# Revit family: BAS-IP_Вызывная панель_AV-04AFDI
name_source: partatom
category: Устройства связи
units: mm (PartAtom-declared; Revit-internal decimal feet)

## family parameters
Всегда вертикально = Да
На основе рабочей плоскости = Нет
Общий = Нет
При загрузке вырезать с полостями = Нет
Размер круглого соединителя = Использовать диаметр
Сохранять ориентацию аннотаций = Нет
Тип детали = Нормальный
Точка расчета площади = Нет

## types (3) — shared parameters
ADSK_Единица измерения = шт.
ADSK_Завод-изготовитель = BAS-IP
ADSK_Количество = 1
ADSK_Наименование = Индивидуальная панель с возможностью подключения индукционной петли
IK-код = IK08
Дисплей = Нет
Изготовитель = BAS-IP
Класс степени защиты = IP65
Корпус = Алюминий
Питание = IEEE 803.2af PoE, +12 В постоянного тока
Потребление питания = 6,5 Вт, в режиме ожидания - 3,6 Вт
Размер под установку = 85 × 180 × 45 мм
Размер самой панели = 95 x 190 x 27 мм
Температурный режим = -40 – +65 °С
Тип панели = Индивидуальная
Тип установки = Скрытого монтажа

## per-type parameters (varying)
| type | ADSK_Марка | ADSK_Материал |
| Серебристый | AV-04AFDI Silver | Silver |
| Красный | AV-04AFDI Red | Red silver |
| Зеленый | AV-04AFDI Green | Green silver |

note: column(s) folded — value = type name in every type: Цветовое решение
